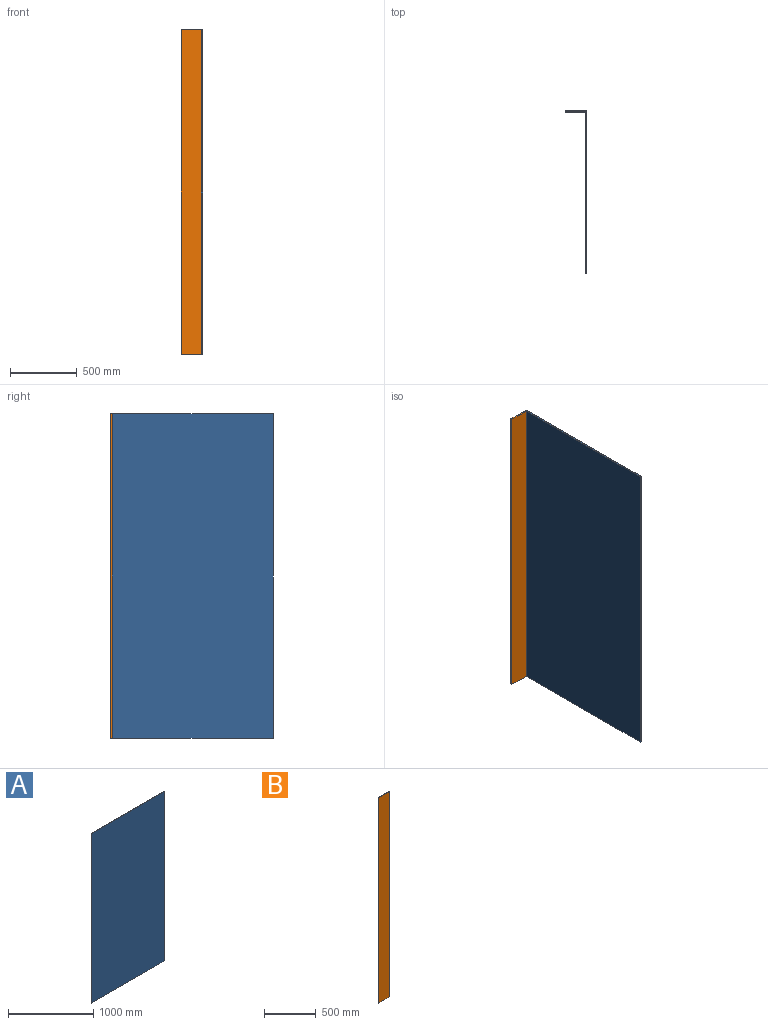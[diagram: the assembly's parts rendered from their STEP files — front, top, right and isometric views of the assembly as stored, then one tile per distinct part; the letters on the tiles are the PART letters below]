
ASSEMBLY  parts=2 mates=1
PART A: 6 faces, bbox 1219.2x9.9x2438.4 mm
  f0: plane 2438.4x9.92mm, normal (1,0,0), area 24193.5mm2, adj f1,f3,f4,f5
  f1: plane 1219.2x9.92mm, normal (0,0,1), area 12096.8mm2, adj f0,f2,f4,f5
  f2: plane 2438.4x9.92mm, normal (-1,0,0), area 24193.5mm2, adj f1,f3,f4,f5
  f3: plane 1219.2x9.92mm, normal (0,0,-1), area 12096.8mm2, adj f0,f2,f4,f5
  f4: plane 2438.4x1219.2mm, normal (0,-1,0), area 2972897.3mm2, adj f0,f1,f2,f3
  f5: plane 2438.4x1219.2mm, normal (0,1,0), area 2972897.3mm2, adj f0,f1,f2,f3
PART B: 6 faces, bbox 152.4x9.9x2438.4 mm
  f0: plane 2438.4x9.92mm, normal (1,0,0), area 24193.5mm2, adj f1,f3,f4,f5
  f1: plane 152.4x9.92mm, normal (0,0,1), area 1512.1mm2, adj f0,f2,f4,f5
  f2: plane 2438.4x9.92mm, normal (-1,0,0), area 24193.5mm2, adj f1,f3,f4,f5
  f3: plane 152.4x9.92mm, normal (0,0,-1), area 1512.1mm2, adj f0,f2,f4,f5
  f4: plane 2438.4x152.4mm, normal (0,-1,0), area 371612.2mm2, adj f0,f1,f2,f3
  f5: plane 2438.4x152.4mm, normal (0,1,0), area 371612.2mm2, adj f0,f1,f2,f3
PLACE A rot(axis=(0.71,-0.71,0),180deg) t=(-1525.07,-519.04,2922.4)mm
PLACE B t=(-1606.23,85.6,2922.4)mm
MATE planar A.f5 <-> B.f0  axis (-1,0,0) through (-1530.03,90.56,1703.2)mm
